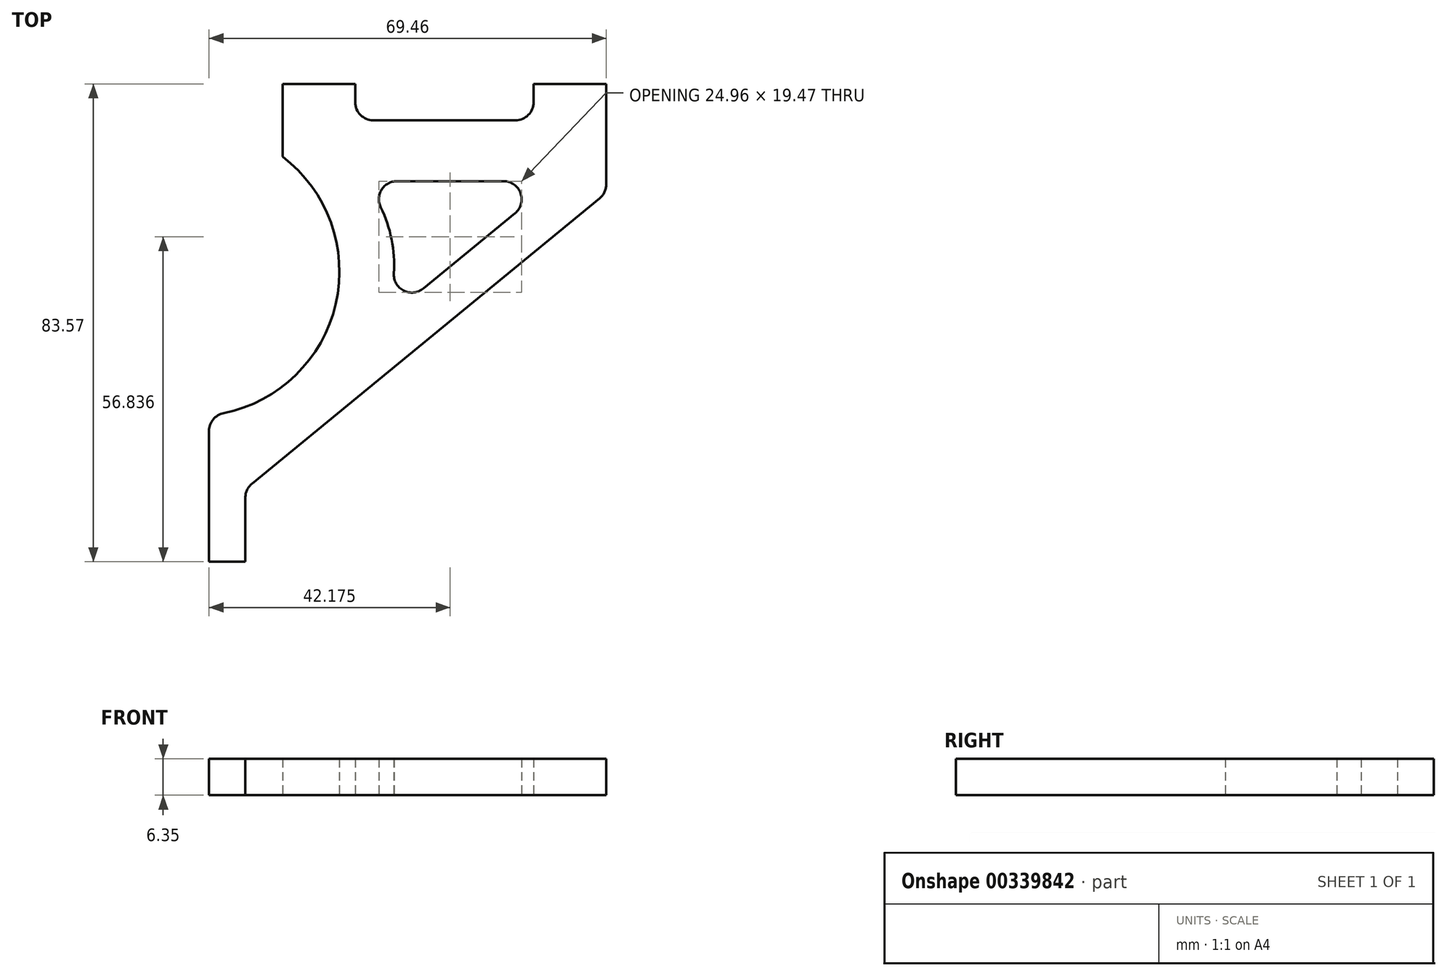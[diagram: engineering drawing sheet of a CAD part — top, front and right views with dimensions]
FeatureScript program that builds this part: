
annotation { "Feature Type Name" : "Feature", "Feature Type Description" : "" }
export const myFeature = defineFeature(function(context is Context, id is Id, definition is map)
    precondition{}
    {
        {
            var Q0;
            Q0=qCreatedBy(makeId("Top.planeOp"),FACE);
            var sketch = newSketch(context, id + "F0", { "sketchPlane" : qUnion([Q0])});
            skLineSegment(sketch, "E0.bottom", {"start": v(-26.18, 26.66) * mm, "end": v(-13.48, 26.66) * mm});
            skLineSegment(sketch, "E0.right", {"start": v(30.44, 26.66) * mm, "end": v(30.44, 9.11) * mm});
            skLineSegment(sketch, "E1.bottom", {"start": v(-32.67, -56.9) * mm, "end": v(-39.02, -56.9) * mm});
            skLineSegment(sketch, "E1.right", {"start": v(-39.02, -56.9) * mm, "end": v(-39.02, -44.2) * mm});
            skPoint(sketch, "E2", {"position": v(-13.48, 26.66) * mm});
            skPoint(sketch, "E3", {"position": v(17.74, 26.66) * mm});
            skPoint(sketch, "E4", {"position": v(-13.48, 20.3) * mm});
            skPoint(sketch, "E5", {"position": v(17.74, 20.3) * mm});
            skLineSegment(sketch, "E6", {"start": v(-13.48, 26.66) * mm, "end": v(-13.48, 23.48) * mm});
            skLineSegment(sketch, "E7", {"start": v(14.56, 20.3) * mm, "end": v(-10.3, 20.3) * mm});
            skLineSegment(sketch, "E8", {"start": v(17.74, 23.48) * mm, "end": v(17.74, 26.66) * mm});
            skLineSegment(sketch, "E9.trimOffspring", {"start": v(17.74, 26.66) * mm, "end": v(30.44, 26.66) * mm});
            skPoint(sketch, "E10", {"position": v(-32.67, -56.9) * mm});
            skLineSegment(sketch, "E11", {"start": v(-32.67, -56.9) * mm, "end": v(-32.67, -45.7) * mm});
            skPoint(sketch, "E12", {"position": v(30.44, 7.6) * mm});
            skLineSegment(sketch, "E13", {"start": v(-26.18, 26.66) * mm, "end": v(-26.18, 13.96) * mm});
            skPoint(sketch, "E14.orphan", {"position": v(-26.18, -56.9) * mm});
            skLineSegment(sketch, "E15", {"start": v(29.28, 6.66) * mm, "end": v(-31.51, -43.24) * mm});
            skLineSegment(sketch, "E16", {"start": v(-39.02, -44.2) * mm, "end": v(-39.02, -34.04) * mm});
            skArc(sketch, "E17", {"start": v(-36.48, -30.93) * mm, "mid": v(-16.87, -11.8) * mm, "end": v(-26.18, 13.96) * mm});
            skPoint(sketch, "E18", {"position": v(-16.7, 13.96) * mm});
            skArc(sketch, "E19", {"start": v(-6.71, -6.45) * mm, "mid": v(-7.1, -0.53) * mm, "end": v(-9, 5.09) * mm});
            skPoint(sketch, "E20.orphan", {"position": v(30.44, 17.13) * mm});
            skLineSegment(sketch, "E21", {"start": v(-6.15, 9.66) * mm, "end": v(12.46, 9.66) * mm});
            skLineSegment(sketch, "E22", {"start": v(-1.53, -9.1) * mm, "end": v(14.48, 4.03) * mm});
            skPoint(sketch, "E23.visualSharp", {"position": v(-32.67, -44.2) * mm});
            skArc(sketch, "E23.filletArc", {"start": v(-31.51, -43.24) * mm, "mid": v(-32.37, -44.34) * mm, "end": v(-32.67, -45.7) * mm});
            skArc(sketch, "E24.filletArc", {"start": v(29.28, 6.66) * mm, "mid": v(30.13, 7.75) * mm, "end": v(30.44, 9.11) * mm});
            skPoint(sketch, "E25.visualSharp", {"position": v(-9.14, -15.35) * mm});
            skArc(sketch, "E25.filletArc", {"start": v(-6.71, -6.45) * mm, "mid": v(-5, -9.48) * mm, "end": v(-1.53, -9.1) * mm});
            skPoint(sketch, "E26.visualSharp", {"position": v(-11.96, 9.66) * mm});
            skArc(sketch, "E26.filletArc", {"start": v(-6.15, 9.66) * mm, "mid": v(-8.85, 8.17) * mm, "end": v(-9, 5.09) * mm});
            skPoint(sketch, "E27.visualSharp", {"position": v(21.33, 9.66) * mm});
            skArc(sketch, "E27.filletArc", {"start": v(14.48, 4.03) * mm, "mid": v(15.45, 7.56) * mm, "end": v(12.46, 9.66) * mm});
            skArc(sketch, "E28.filletArc", {"start": v(-13.48, 23.48) * mm, "mid": v(-12.55, 21.24) * mm, "end": v(-10.3, 20.3) * mm});
            skArc(sketch, "E29.filletArc", {"start": v(14.56, 20.3) * mm, "mid": v(16.8, 21.24) * mm, "end": v(17.74, 23.48) * mm});
            skPoint(sketch, "E30.visualSharp", {"position": v(-39.02, -31.31) * mm});
            skArc(sketch, "E30.filletArc", {"start": v(-36.48, -30.93) * mm, "mid": v(-38.3, -32.03) * mm, "end": v(-39.02, -34.04) * mm});
            skSolve(sketch);
        }
        {
            var Q0;
            Q0=makeQuery(id+"F0.imprint","IMPRINT",FACE,{"disambiguationData":[TD([[makeQuery(id+"F0.imprint","IMPRINT",EDGE,{"derivedFrom":sQuery(id+"F0.wireOp",EDGE,"E0.bottom")}),-1.0]])]});
            extrude(context, id + "F1", {"entities" : qUnion([Q0]), "depth" : 6.35 * mm});
        }
    });
